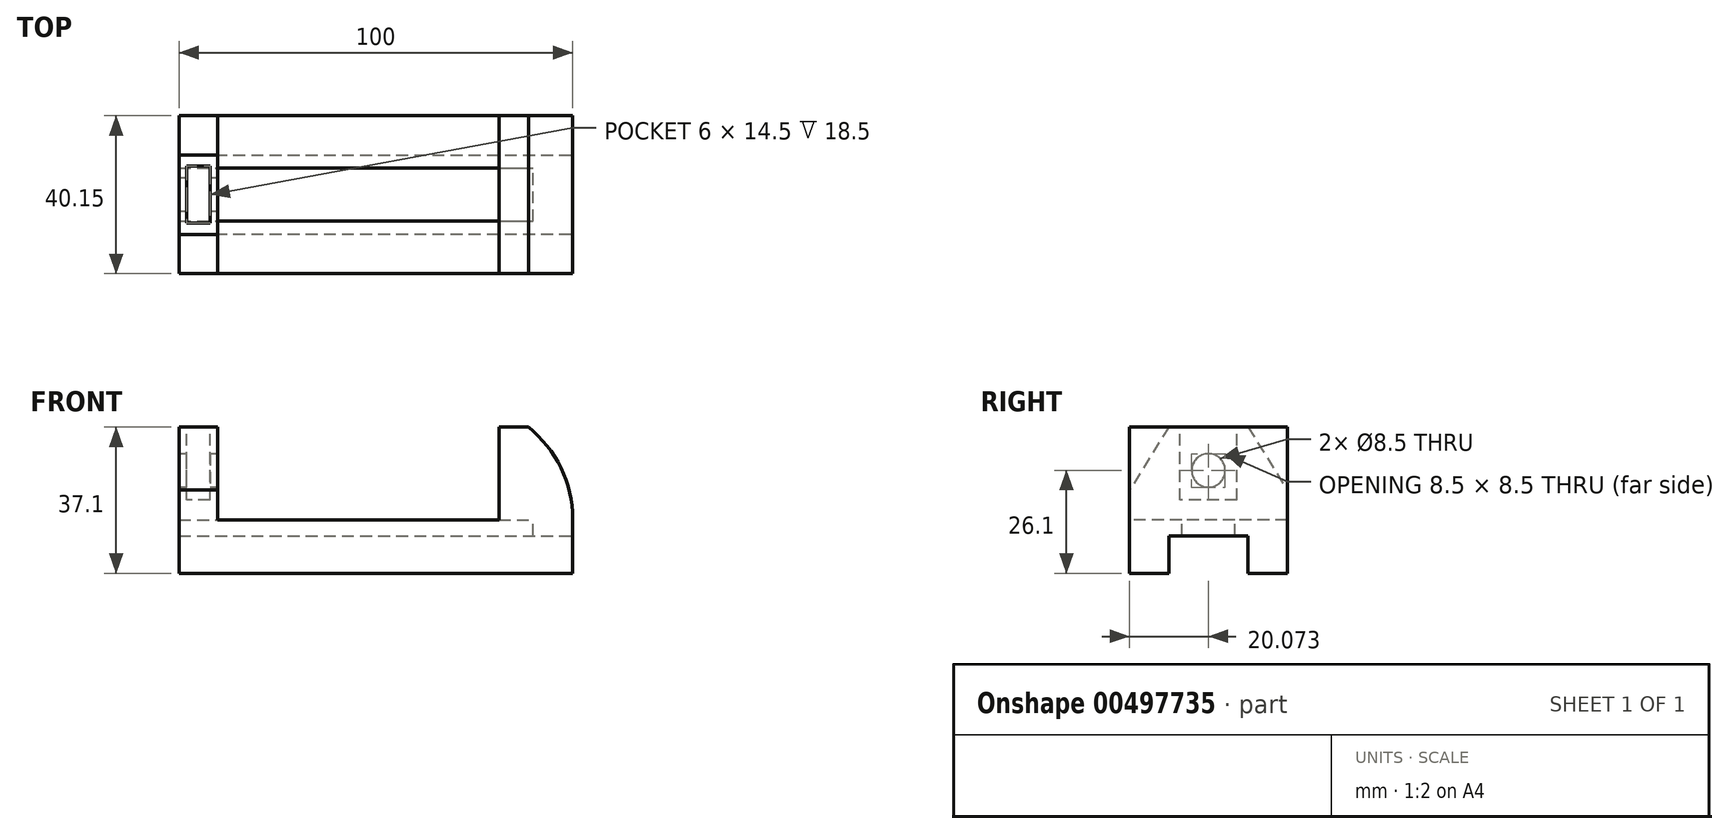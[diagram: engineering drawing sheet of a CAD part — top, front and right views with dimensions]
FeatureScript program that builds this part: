
annotation { "Feature Type Name" : "Feature", "Feature Type Description" : "" }
export const myFeature = defineFeature(function(context is Context, id is Id, definition is map)
    precondition{}
    {
        {
            var Q0;
            Q0=qCreatedBy(makeId("Top.planeOp"),FACE);
            var sketch = newSketch(context, id + "F0", { "sketchPlane" : qUnion([Q0])});
            skLineSegment(sketch, "E0.bottom", {"start": v(-62.81, 16.45) * mm, "end": v(37.19, 16.45) * mm});
            skLineSegment(sketch, "E0.top", {"start": v(-62.81, -23.7) * mm, "end": v(37.19, -23.7) * mm});
            skLineSegment(sketch, "E0.left", {"start": v(-62.81, 16.45) * mm, "end": v(-62.81, -23.7) * mm});
            skLineSegment(sketch, "E0.right", {"start": v(37.19, 16.45) * mm, "end": v(37.19, -23.7) * mm});
            skLineSegment(sketch, "E1", {"start": v(-62.81, -3.63) * mm, "end": v(37.19, -3.63) * mm, "construction": true});
            skLineSegment(sketch, "E2", {"start": v(-62.81, -3.63) * mm, "end": v(-62.81, 6.42) * mm, "construction": true});
            skLineSegment(sketch, "E3", {"start": v(-62.81, 6.42) * mm, "end": v(37.19, 6.42) * mm});
            skLineSegment(sketch, "E4", {"start": v(-62.81, 16.45) * mm, "end": v(-62.81, 3.12) * mm, "construction": true});
            skLineSegment(sketch, "E5", {"start": v(-62.81, 3.12) * mm, "end": v(37.19, 3.12) * mm});
            skLineSegment(sketch, "E6", {"start": v(-62.81, -3.63) * mm, "end": v(-53.01, -3.63) * mm, "construction": true});
            skLineSegment(sketch, "E7", {"start": v(-53.01, -3.63) * mm, "end": v(-53.01, 16.45) * mm});
            skLineSegment(sketch, "E8", {"start": v(37.19, -3.63) * mm, "end": v(18.44, -3.63) * mm, "construction": true});
            skLineSegment(sketch, "E9", {"start": v(18.44, -3.63) * mm, "end": v(18.44, 16.45) * mm});
            skLineSegment(sketch, "E10.MirrorCS", {"start": v(18.44, -3.63) * mm, "end": v(18.44, -23.7) * mm});
            skLineSegment(sketch, "E11.MirrorCS", {"start": v(-53.01, -3.63) * mm, "end": v(-53.01, -23.7) * mm});
            skLineSegment(sketch, "E12.MirrorCS", {"start": v(-62.81, -10.37) * mm, "end": v(37.19, -10.37) * mm});
            skLineSegment(sketch, "E13.MirrorCS", {"start": v(-62.81, -13.68) * mm, "end": v(37.19, -13.68) * mm});
            skLineSegment(sketch, "E14", {"start": v(37.19, -3.63) * mm, "end": v(27.19, -3.63) * mm, "construction": true});
            skLineSegment(sketch, "E15", {"start": v(27.19, -3.63) * mm, "end": v(27.19, -23.7) * mm});
            skLineSegment(sketch, "E16.MirrorCS", {"start": v(27.19, -3.63) * mm, "end": v(27.19, 16.45) * mm});
            skSolve(sketch);
        }
        {
            var Q0;
            {var subQ0=sQuery(id+"F0.wireOp",EDGE,"E12.MirrorCS");var subQ1=sQuery(id+"F0.wireOp",EDGE,"E0.right");var subQ2=makeQuery(id+"F0.imprint","INTERSECT",VERTEX,{"derivedFrom":[subQ1,subQ0]});Q0=makeQuery(id+"F0.imprint","IMPRINT",FACE,{"disambiguationData":[TD([[makeQuery(id+"F0.imprint","IMPRINT",EDGE,{"disambiguationData":[TD([[subQ2,-1.0]])],"derivedFrom":subQ1}),-1.0]])]});}
            var Q1;
            {var subQ0=sQuery(id+"F0.wireOp",EDGE,"E12.MirrorCS");var subQ1=sQuery(id+"F0.wireOp",EDGE,"E10.MirrorCS");var subQ2=makeQuery(id+"F0.imprint","INTERSECT",VERTEX,{"derivedFrom":[subQ1,subQ0]});Q1=makeQuery(id+"F0.imprint","IMPRINT",FACE,{"disambiguationData":[TD([[makeQuery(id+"F0.imprint","IMPRINT",EDGE,{"disambiguationData":[TD([[subQ2,-1.0]])],"derivedFrom":subQ1}),-1.0]])]});}
            var Q2;
            {var subQ0=sQuery(id+"F0.wireOp",EDGE,"E12.MirrorCS");var subQ1=sQuery(id+"F0.wireOp",EDGE,"E10.MirrorCS");var subQ2=makeQuery(id+"F0.imprint","INTERSECT",VERTEX,{"derivedFrom":[subQ1,subQ0]});Q2=makeQuery(id+"F0.imprint","IMPRINT",FACE,{"disambiguationData":[TD([[makeQuery(id+"F0.imprint","IMPRINT",EDGE,{"disambiguationData":[TD([[subQ2,-1.0]])],"derivedFrom":subQ1}),1.0]])]});}
            var Q3;
            {var subQ0=sQuery(id+"F0.wireOp",EDGE,"E10.MirrorCS");var subQ1=sQuery(id+"F0.wireOp",EDGE,"E0.top");var subQ2=makeQuery(id+"F0.imprint","INTERSECT",VERTEX,{"derivedFrom":[subQ1,subQ0]});Q3=makeQuery(id+"F0.imprint","IMPRINT",FACE,{"disambiguationData":[TD([[makeQuery(id+"F0.imprint","IMPRINT",EDGE,{"disambiguationData":[TD([[subQ2,-1.0]])],"derivedFrom":subQ1}),1.0]])]});}
            var Q4;
            {var subQ0=sQuery(id+"F0.wireOp",EDGE,"E0.right");var subQ1=sQuery(id+"F0.wireOp",EDGE,"E0.top");var subQ2=makeQuery(id+"F0.imprint","INTERSECT",VERTEX,{"derivedFrom":[subQ1,subQ0]});Q4=makeQuery(id+"F0.imprint","IMPRINT",FACE,{"disambiguationData":[TD([[makeQuery(id+"F0.imprint","IMPRINT",EDGE,{"disambiguationData":[TD([[subQ2,1.0]])],"derivedFrom":subQ1}),1.0]])]});}
            var Q5;
            {var subQ0=sQuery(id+"F0.wireOp",EDGE,"E10.MirrorCS");var subQ1=sQuery(id+"F0.wireOp",EDGE,"E0.top");var subQ2=makeQuery(id+"F0.imprint","INTERSECT",VERTEX,{"derivedFrom":[subQ1,subQ0]});Q5=makeQuery(id+"F0.imprint","IMPRINT",FACE,{"disambiguationData":[TD([[makeQuery(id+"F0.imprint","IMPRINT",EDGE,{"disambiguationData":[TD([[subQ2,1.0]])],"derivedFrom":subQ1}),1.0]])]});}
            var Q6;
            {var subQ0=sQuery(id+"F0.wireOp",EDGE,"E0.left");var subQ1=sQuery(id+"F0.wireOp",EDGE,"E0.top");var subQ2=makeQuery(id+"F0.imprint","INTERSECT",VERTEX,{"derivedFrom":[subQ1,subQ0]});Q6=makeQuery(id+"F0.imprint","IMPRINT",FACE,{"disambiguationData":[TD([[makeQuery(id+"F0.imprint","IMPRINT",EDGE,{"disambiguationData":[TD([[subQ2,-1.0]])],"derivedFrom":subQ1}),1.0]])]});}
            var Q7;
            {var subQ0=sQuery(id+"F0.wireOp",EDGE,"E12.MirrorCS");var subQ1=sQuery(id+"F0.wireOp",EDGE,"E0.left");var subQ2=makeQuery(id+"F0.imprint","INTERSECT",VERTEX,{"derivedFrom":[subQ1,subQ0]});Q7=makeQuery(id+"F0.imprint","IMPRINT",FACE,{"disambiguationData":[TD([[makeQuery(id+"F0.imprint","IMPRINT",EDGE,{"disambiguationData":[TD([[subQ2,-1.0]])],"derivedFrom":subQ1}),1.0]])]});}
            var Q8;
            {var subQ0=sQuery(id+"F0.wireOp",EDGE,"E3");var subQ1=sQuery(id+"F0.wireOp",EDGE,"E0.left");var subQ2=makeQuery(id+"F0.imprint","INTERSECT",VERTEX,{"derivedFrom":[subQ1,subQ0]});Q8=makeQuery(id+"F0.imprint","IMPRINT",FACE,{"disambiguationData":[TD([[makeQuery(id+"F0.imprint","IMPRINT",EDGE,{"disambiguationData":[TD([[subQ2,-1.0]])],"derivedFrom":subQ1}),1.0]])]});}
            var Q9;
            {var subQ0=sQuery(id+"F0.wireOp",EDGE,"E0.left");var subQ1=sQuery(id+"F0.wireOp",EDGE,"E0.bottom");var subQ2=makeQuery(id+"F0.imprint","INTERSECT",VERTEX,{"derivedFrom":[subQ1,subQ0]});Q9=makeQuery(id+"F0.imprint","IMPRINT",FACE,{"disambiguationData":[TD([[makeQuery(id+"F0.imprint","IMPRINT",EDGE,{"disambiguationData":[TD([[subQ2,-1.0]])],"derivedFrom":subQ1}),-1.0]])]});}
            var Q10;
            {var subQ0=sQuery(id+"F0.wireOp",EDGE,"E7");var subQ1=sQuery(id+"F0.wireOp",EDGE,"E0.bottom");var subQ2=makeQuery(id+"F0.imprint","INTERSECT",VERTEX,{"derivedFrom":[subQ1,subQ0]});Q10=makeQuery(id+"F0.imprint","IMPRINT",FACE,{"disambiguationData":[TD([[makeQuery(id+"F0.imprint","IMPRINT",EDGE,{"disambiguationData":[TD([[subQ2,-1.0]])],"derivedFrom":subQ1}),-1.0]])]});}
            var Q11;
            {var subQ0=sQuery(id+"F0.wireOp",EDGE,"E7");var subQ1=sQuery(id+"F0.wireOp",EDGE,"E3");var subQ2=makeQuery(id+"F0.imprint","INTERSECT",VERTEX,{"derivedFrom":[subQ1,subQ0]});Q11=makeQuery(id+"F0.imprint","IMPRINT",FACE,{"disambiguationData":[TD([[makeQuery(id+"F0.imprint","IMPRINT",EDGE,{"disambiguationData":[TD([[subQ2,-1.0]])],"derivedFrom":subQ1}),-1.0]])]});}
            var Q12;
            {var subQ0=sQuery(id+"F0.wireOp",EDGE,"E9");var subQ1=sQuery(id+"F0.wireOp",EDGE,"E0.bottom");var subQ2=makeQuery(id+"F0.imprint","INTERSECT",VERTEX,{"derivedFrom":[subQ1,subQ0]});Q12=makeQuery(id+"F0.imprint","IMPRINT",FACE,{"disambiguationData":[TD([[makeQuery(id+"F0.imprint","IMPRINT",EDGE,{"disambiguationData":[TD([[subQ2,-1.0]])],"derivedFrom":subQ1}),-1.0]])]});}
            var Q13;
            {var subQ0=sQuery(id+"F0.wireOp",EDGE,"E9");var subQ1=sQuery(id+"F0.wireOp",EDGE,"E3");var subQ2=makeQuery(id+"F0.imprint","INTERSECT",VERTEX,{"derivedFrom":[subQ1,subQ0]});Q13=makeQuery(id+"F0.imprint","IMPRINT",FACE,{"disambiguationData":[TD([[makeQuery(id+"F0.imprint","IMPRINT",EDGE,{"disambiguationData":[TD([[subQ2,-1.0]])],"derivedFrom":subQ1}),-1.0]])]});}
            var Q14;
            {var subQ0=sQuery(id+"F0.wireOp",EDGE,"E3");var subQ1=sQuery(id+"F0.wireOp",EDGE,"E0.right");var subQ2=makeQuery(id+"F0.imprint","INTERSECT",VERTEX,{"derivedFrom":[subQ1,subQ0]});Q14=makeQuery(id+"F0.imprint","IMPRINT",FACE,{"disambiguationData":[TD([[makeQuery(id+"F0.imprint","IMPRINT",EDGE,{"disambiguationData":[TD([[subQ2,-1.0]])],"derivedFrom":subQ1}),-1.0]])]});}
            var Q15;
            {var subQ0=sQuery(id+"F0.wireOp",EDGE,"E0.right");var subQ1=sQuery(id+"F0.wireOp",EDGE,"E0.bottom");var subQ2=makeQuery(id+"F0.imprint","INTERSECT",VERTEX,{"derivedFrom":[subQ1,subQ0]});Q15=makeQuery(id+"F0.imprint","IMPRINT",FACE,{"disambiguationData":[TD([[makeQuery(id+"F0.imprint","IMPRINT",EDGE,{"disambiguationData":[TD([[subQ2,1.0]])],"derivedFrom":subQ1}),-1.0]])]});}
            var Q16;
            {var subQ5=sQuery(id+"F0.wireOp",EDGE,"E0.right");var subQ7=sQuery(id+"F0.wireOp",EDGE,"E5");var subQ8=makeQuery(id+"F0.imprint","INTERSECT",VERTEX,{"derivedFrom":[subQ5,subQ7]});Q16=makeQuery(id+"F0.imprint","IMPRINT",FACE,{"disambiguationData":[TD([[makeQuery(id+"F0.imprint","IMPRINT",EDGE,{"disambiguationData":[TD([[subQ8,-1.0]])],"derivedFrom":subQ5}),-1.0]])]});}
            extrude(context, id + "F1", {"entities" : qUnion([Q0, Q1, Q2, Q3, Q4, Q5, Q6, Q7, Q8, Q9, Q10, Q11, Q12, Q13, Q14, Q15, Q16]), "oppositeDirection" : true, "depth" : 4 * mm});
        }
        {
            var Q0;
            {var subQ0=sQuery(id+"F0.wireOp",EDGE,"E0.left");var subQ1=sQuery(id+"F0.wireOp",EDGE,"E0.top");var subQ2=makeQuery(id+"F0.imprint","INTERSECT",VERTEX,{"derivedFrom":[subQ1,subQ0]});Q0=makeQuery(id+"F0.imprint","IMPRINT",FACE,{"disambiguationData":[TD([[makeQuery(id+"F0.imprint","IMPRINT",EDGE,{"disambiguationData":[TD([[subQ2,-1.0]])],"derivedFrom":subQ1}),1.0]])]});}
            var Q1;
            {var subQ0=sQuery(id+"F0.wireOp",EDGE,"E10.MirrorCS");var subQ1=sQuery(id+"F0.wireOp",EDGE,"E0.top");var subQ2=makeQuery(id+"F0.imprint","INTERSECT",VERTEX,{"derivedFrom":[subQ1,subQ0]});Q1=makeQuery(id+"F0.imprint","IMPRINT",FACE,{"disambiguationData":[TD([[makeQuery(id+"F0.imprint","IMPRINT",EDGE,{"disambiguationData":[TD([[subQ2,1.0]])],"derivedFrom":subQ1}),1.0]])]});}
            var Q2;
            {var subQ0=sQuery(id+"F0.wireOp",EDGE,"E10.MirrorCS");var subQ1=sQuery(id+"F0.wireOp",EDGE,"E0.top");var subQ2=makeQuery(id+"F0.imprint","INTERSECT",VERTEX,{"derivedFrom":[subQ1,subQ0]});Q2=makeQuery(id+"F0.imprint","IMPRINT",FACE,{"disambiguationData":[TD([[makeQuery(id+"F0.imprint","IMPRINT",EDGE,{"disambiguationData":[TD([[subQ2,-1.0]])],"derivedFrom":subQ1}),1.0]])]});}
            var Q3;
            {var subQ0=sQuery(id+"F0.wireOp",EDGE,"E0.right");var subQ1=sQuery(id+"F0.wireOp",EDGE,"E0.top");var subQ2=makeQuery(id+"F0.imprint","INTERSECT",VERTEX,{"derivedFrom":[subQ1,subQ0]});Q3=makeQuery(id+"F0.imprint","IMPRINT",FACE,{"disambiguationData":[TD([[makeQuery(id+"F0.imprint","IMPRINT",EDGE,{"disambiguationData":[TD([[subQ2,1.0]])],"derivedFrom":subQ1}),1.0]])]});}
            var Q4;
            {var subQ0=sQuery(id+"F0.wireOp",EDGE,"E0.right");var subQ1=sQuery(id+"F0.wireOp",EDGE,"E0.bottom");var subQ2=makeQuery(id+"F0.imprint","INTERSECT",VERTEX,{"derivedFrom":[subQ1,subQ0]});Q4=makeQuery(id+"F0.imprint","IMPRINT",FACE,{"disambiguationData":[TD([[makeQuery(id+"F0.imprint","IMPRINT",EDGE,{"disambiguationData":[TD([[subQ2,1.0]])],"derivedFrom":subQ1}),-1.0]])]});}
            var Q5;
            {var subQ0=sQuery(id+"F0.wireOp",EDGE,"E9");var subQ1=sQuery(id+"F0.wireOp",EDGE,"E0.bottom");var subQ2=makeQuery(id+"F0.imprint","INTERSECT",VERTEX,{"derivedFrom":[subQ1,subQ0]});Q5=makeQuery(id+"F0.imprint","IMPRINT",FACE,{"disambiguationData":[TD([[makeQuery(id+"F0.imprint","IMPRINT",EDGE,{"disambiguationData":[TD([[subQ2,-1.0]])],"derivedFrom":subQ1}),-1.0]])]});}
            var Q6;
            {var subQ0=sQuery(id+"F0.wireOp",EDGE,"E7");var subQ1=sQuery(id+"F0.wireOp",EDGE,"E0.bottom");var subQ2=makeQuery(id+"F0.imprint","INTERSECT",VERTEX,{"derivedFrom":[subQ1,subQ0]});Q6=makeQuery(id+"F0.imprint","IMPRINT",FACE,{"disambiguationData":[TD([[makeQuery(id+"F0.imprint","IMPRINT",EDGE,{"disambiguationData":[TD([[subQ2,-1.0]])],"derivedFrom":subQ1}),-1.0]])]});}
            var Q7;
            {var subQ0=sQuery(id+"F0.wireOp",EDGE,"E0.left");var subQ1=sQuery(id+"F0.wireOp",EDGE,"E0.bottom");var subQ2=makeQuery(id+"F0.imprint","INTERSECT",VERTEX,{"derivedFrom":[subQ1,subQ0]});Q7=makeQuery(id+"F0.imprint","IMPRINT",FACE,{"disambiguationData":[TD([[makeQuery(id+"F0.imprint","IMPRINT",EDGE,{"disambiguationData":[TD([[subQ2,-1.0]])],"derivedFrom":subQ1}),-1.0]])]});}
            extrude(context, id + "F2", {"entities" : qUnion([Q0, Q1, Q2, Q3, Q4, Q5, Q6, Q7]), "operationType" : NewBodyOperationType.ADD, "oppositeDirection" : true, "depth" : 13.5 * mm});
        }
        {
            var Q0;
            {var subQ3=sQuery(id+"F0.wireOp",EDGE,"E5");var subQ5=sQuery(id+"F0.wireOp",EDGE,"E0.left");var subQ6=makeQuery(id+"F0.imprint","INTERSECT",VERTEX,{"derivedFrom":[subQ5,subQ3]});Q0=makeQuery(id+"F0.imprint","IMPRINT",FACE,{"disambiguationData":[TD([[makeQuery(id+"F0.imprint","IMPRINT",EDGE,{"disambiguationData":[TD([[subQ6,-1.0]])],"derivedFrom":subQ5}),1.0]])]});}
            var Q1;
            {var subQ0=sQuery(id+"F0.wireOp",EDGE,"E12.MirrorCS");var subQ1=sQuery(id+"F0.wireOp",EDGE,"E0.left");var subQ2=makeQuery(id+"F0.imprint","INTERSECT",VERTEX,{"derivedFrom":[subQ1,subQ0]});Q1=makeQuery(id+"F0.imprint","IMPRINT",FACE,{"disambiguationData":[TD([[makeQuery(id+"F0.imprint","IMPRINT",EDGE,{"disambiguationData":[TD([[subQ2,-1.0]])],"derivedFrom":subQ1}),1.0]])]});}
            var Q2;
            {var subQ0=sQuery(id+"F0.wireOp",EDGE,"E0.left");var subQ1=sQuery(id+"F0.wireOp",EDGE,"E0.top");var subQ2=makeQuery(id+"F0.imprint","INTERSECT",VERTEX,{"derivedFrom":[subQ1,subQ0]});Q2=makeQuery(id+"F0.imprint","IMPRINT",FACE,{"disambiguationData":[TD([[makeQuery(id+"F0.imprint","IMPRINT",EDGE,{"disambiguationData":[TD([[subQ2,-1.0]])],"derivedFrom":subQ1}),1.0]])]});}
            var Q3;
            {var subQ0=sQuery(id+"F0.wireOp",EDGE,"E3");var subQ1=sQuery(id+"F0.wireOp",EDGE,"E0.left");var subQ2=makeQuery(id+"F0.imprint","INTERSECT",VERTEX,{"derivedFrom":[subQ1,subQ0]});Q3=makeQuery(id+"F0.imprint","IMPRINT",FACE,{"disambiguationData":[TD([[makeQuery(id+"F0.imprint","IMPRINT",EDGE,{"disambiguationData":[TD([[subQ2,-1.0]])],"derivedFrom":subQ1}),1.0]])]});}
            var Q4;
            {var subQ0=sQuery(id+"F0.wireOp",EDGE,"E0.left");var subQ1=sQuery(id+"F0.wireOp",EDGE,"E0.bottom");var subQ2=makeQuery(id+"F0.imprint","INTERSECT",VERTEX,{"derivedFrom":[subQ1,subQ0]});Q4=makeQuery(id+"F0.imprint","IMPRINT",FACE,{"disambiguationData":[TD([[makeQuery(id+"F0.imprint","IMPRINT",EDGE,{"disambiguationData":[TD([[subQ2,-1.0]])],"derivedFrom":subQ1}),-1.0]])]});}
            var Q5;
            {var subQ0=sQuery(id+"F0.wireOp",EDGE,"E0.right");var subQ1=sQuery(id+"F0.wireOp",EDGE,"E0.bottom");var subQ2=makeQuery(id+"F0.imprint","INTERSECT",VERTEX,{"derivedFrom":[subQ1,subQ0]});Q5=makeQuery(id+"F0.imprint","IMPRINT",FACE,{"disambiguationData":[TD([[makeQuery(id+"F0.imprint","IMPRINT",EDGE,{"disambiguationData":[TD([[subQ2,1.0]])],"derivedFrom":subQ1}),-1.0]])]});}
            var Q6;
            {var subQ0=sQuery(id+"F0.wireOp",EDGE,"E9");var subQ1=sQuery(id+"F0.wireOp",EDGE,"E3");var subQ2=makeQuery(id+"F0.imprint","INTERSECT",VERTEX,{"derivedFrom":[subQ1,subQ0]});Q6=makeQuery(id+"F0.imprint","IMPRINT",FACE,{"disambiguationData":[TD([[makeQuery(id+"F0.imprint","IMPRINT",EDGE,{"disambiguationData":[TD([[subQ2,-1.0]])],"derivedFrom":subQ1}),-1.0]])]});}
            var Q7;
            {var subQ0=sQuery(id+"F0.wireOp",EDGE,"E9");var subQ1=sQuery(id+"F0.wireOp",EDGE,"E0.bottom");var subQ2=makeQuery(id+"F0.imprint","INTERSECT",VERTEX,{"derivedFrom":[subQ1,subQ0]});Q7=makeQuery(id+"F0.imprint","IMPRINT",FACE,{"disambiguationData":[TD([[makeQuery(id+"F0.imprint","IMPRINT",EDGE,{"disambiguationData":[TD([[subQ2,-1.0]])],"derivedFrom":subQ1}),-1.0]])]});}
            var Q8;
            {var subQ5=sQuery(id+"F0.wireOp",EDGE,"E9");var subQ7=sQuery(id+"F0.wireOp",EDGE,"E5");var subQ8=makeQuery(id+"F0.imprint","INTERSECT",VERTEX,{"derivedFrom":[subQ7,subQ5]});Q8=makeQuery(id+"F0.imprint","IMPRINT",FACE,{"disambiguationData":[TD([[makeQuery(id+"F0.imprint","IMPRINT",EDGE,{"disambiguationData":[TD([[subQ8,-1.0]])],"derivedFrom":subQ7}),-1.0]])]});}
            var Q9;
            {var subQ0=sQuery(id+"F0.wireOp",EDGE,"E10.MirrorCS");var subQ1=sQuery(id+"F0.wireOp",EDGE,"E0.top");var subQ2=makeQuery(id+"F0.imprint","INTERSECT",VERTEX,{"derivedFrom":[subQ1,subQ0]});Q9=makeQuery(id+"F0.imprint","IMPRINT",FACE,{"disambiguationData":[TD([[makeQuery(id+"F0.imprint","IMPRINT",EDGE,{"disambiguationData":[TD([[subQ2,-1.0]])],"derivedFrom":subQ1}),1.0]])]});}
            var Q10;
            {var subQ0=sQuery(id+"F0.wireOp",EDGE,"E12.MirrorCS");var subQ1=sQuery(id+"F0.wireOp",EDGE,"E10.MirrorCS");var subQ2=makeQuery(id+"F0.imprint","INTERSECT",VERTEX,{"derivedFrom":[subQ1,subQ0]});Q10=makeQuery(id+"F0.imprint","IMPRINT",FACE,{"disambiguationData":[TD([[makeQuery(id+"F0.imprint","IMPRINT",EDGE,{"disambiguationData":[TD([[subQ2,-1.0]])],"derivedFrom":subQ1}),1.0]])]});}
            var Q11;
            {var subQ0=sQuery(id+"F0.wireOp",EDGE,"E0.right");var subQ1=sQuery(id+"F0.wireOp",EDGE,"E0.top");var subQ2=makeQuery(id+"F0.imprint","INTERSECT",VERTEX,{"derivedFrom":[subQ1,subQ0]});Q11=makeQuery(id+"F0.imprint","IMPRINT",FACE,{"disambiguationData":[TD([[makeQuery(id+"F0.imprint","IMPRINT",EDGE,{"disambiguationData":[TD([[subQ2,1.0]])],"derivedFrom":subQ1}),1.0]])]});}
            var Q12;
            {var subQ0=sQuery(id+"F0.wireOp",EDGE,"E12.MirrorCS");var subQ1=sQuery(id+"F0.wireOp",EDGE,"E0.right");var subQ2=makeQuery(id+"F0.imprint","INTERSECT",VERTEX,{"derivedFrom":[subQ1,subQ0]});Q12=makeQuery(id+"F0.imprint","IMPRINT",FACE,{"disambiguationData":[TD([[makeQuery(id+"F0.imprint","IMPRINT",EDGE,{"disambiguationData":[TD([[subQ2,-1.0]])],"derivedFrom":subQ1}),-1.0]])]});}
            var Q13;
            {var subQ5=sQuery(id+"F0.wireOp",EDGE,"E0.right");var subQ7=sQuery(id+"F0.wireOp",EDGE,"E5");var subQ8=makeQuery(id+"F0.imprint","INTERSECT",VERTEX,{"derivedFrom":[subQ5,subQ7]});Q13=makeQuery(id+"F0.imprint","IMPRINT",FACE,{"disambiguationData":[TD([[makeQuery(id+"F0.imprint","IMPRINT",EDGE,{"disambiguationData":[TD([[subQ8,-1.0]])],"derivedFrom":subQ5}),-1.0]])]});}
            var Q14;
            {var subQ0=sQuery(id+"F0.wireOp",EDGE,"E3");var subQ1=sQuery(id+"F0.wireOp",EDGE,"E0.right");var subQ2=makeQuery(id+"F0.imprint","INTERSECT",VERTEX,{"derivedFrom":[subQ1,subQ0]});Q14=makeQuery(id+"F0.imprint","IMPRINT",FACE,{"disambiguationData":[TD([[makeQuery(id+"F0.imprint","IMPRINT",EDGE,{"disambiguationData":[TD([[subQ2,-1.0]])],"derivedFrom":subQ1}),-1.0]])]});}
            extrude(context, id + "F3", {"entities" : qUnion([Q0, Q1, Q2, Q3, Q4, Q5, Q6, Q7, Q8, Q9, Q10, Q11, Q12, Q13, Q14]), "operationType" : NewBodyOperationType.ADD, "depth" : 23.6 * mm});
        }
        {
            var Q0;
            {var subQ0=sQuery(id+"F0.wireOp",EDGE,"E0.bottom");Q0=makeQuery(id+"F3.opExtrude","CAP_EDGE",EDGE,{"disambiguationData":[OSD([subQ0]),TDD([makeQuery(id+"F0.imprint","IMPRINT",EDGE,{"disambiguationData":[TD([[makeQuery(id+"F0.imprint","INTERSECT",VERTEX,{"derivedFrom":[subQ0,sQuery(id+"F0.wireOp",EDGE,"E0.left")]}),-1.0]])],"derivedFrom":subQ0})])],"isStart":false});}
            var Q1;
            {var subQ0=sQuery(id+"F0.wireOp",EDGE,"E0.top");Q1=makeQuery(id+"F3.opExtrude","CAP_EDGE",EDGE,{"disambiguationData":[OSD([subQ0]),TDD([makeQuery(id+"F0.imprint","IMPRINT",EDGE,{"disambiguationData":[TD([[makeQuery(id+"F0.imprint","INTERSECT",VERTEX,{"derivedFrom":[subQ0,sQuery(id+"F0.wireOp",EDGE,"E0.left")]}),-1.0]])],"derivedFrom":subQ0})])],"isStart":false});}
            chamfer(context, id + "F4", {"entities" : qUnion([Q0, Q1]), "chamferType" : ChamferType.TWO_OFFSETS, "width1" : 16 * mm, "oppositeDirection" : false, "width2" : 10 * mm, "tangentPropagation" : true});
        }
        {
            var Q0;
            {var subQ0=sQuery(id+"F0.wireOp",EDGE,"E0.bottom");Q0=makeQuery(id+"F3.boolean.opBoolean","MERGE",FACE,{"derivedFrom":[makeQuery(id+"F2.boolean.opBoolean","MERGE",FACE,{"derivedFrom":[makeQuery(id+"F1.opExtrude","SWEPT_FACE",FACE,{"disambiguationData":[OSD([subQ0])]}),makeQuery(id+"F2.opExtrude","SWEPT_FACE",FACE,{"disambiguationData":[OSD([subQ0])]})]}),makeQuery(id+"F3.opExtrude","SWEPT_FACE",FACE,{"disambiguationData":[OSD([subQ0]),TDD([makeQuery(id+"F0.imprint","IMPRINT",EDGE,{"disambiguationData":[TD([[makeQuery(id+"F0.imprint","INTERSECT",VERTEX,{"derivedFrom":[subQ0,sQuery(id+"F0.wireOp",EDGE,"E0.left")]}),-1.0]])],"derivedFrom":subQ0})])]}),makeQuery(id+"F3.opExtrude","SWEPT_FACE",FACE,{"disambiguationData":[OSD([subQ0]),TDD([makeQuery(id+"F0.imprint","IMPRINT",EDGE,{"disambiguationData":[TD([[makeQuery(id+"F0.imprint","INTERSECT",VERTEX,{"derivedFrom":[subQ0,sQuery(id+"F0.wireOp",EDGE,"E9")]}),-1.0]])],"derivedFrom":subQ0}),makeQuery(id+"F0.imprint","IMPRINT",EDGE,{"disambiguationData":[TD([[makeQuery(id+"F0.imprint","INTERSECT",VERTEX,{"derivedFrom":[subQ0,sQuery(id+"F0.wireOp",EDGE,"E0.right")]}),1.0]])],"derivedFrom":subQ0})])]})]});}
            var sketch = newSketch(context, id + "F5", { "sketchPlane" : qUnion([Q0])});
            skLineSegment(sketch, "E17", {"start": v(-18.44, 23.6) * mm, "end": v(-25.94, 23.6) * mm});
            skArc(sketch, "E18", {"start": v(-25.94, 23.6) * mm, "mid": v(-34.27, 13.09) * mm, "end": v(-37.19, 0) * mm});
            skSolve(sketch);
        }
        {
            var Q0;
            {var subQ0=sQuery(id+"F5.wireOp",EDGE,"E18");var subQ1=sQuery(id+"F0.wireOp",EDGE,"E0.right");var subQ2=sQuery(id+"F0.wireOp",EDGE,"E0.bottom");var subQ4=makeQuery(id+"F3.opExtrude","CAP_EDGE",EDGE,{"disambiguationData":[OSD([subQ2]),TDD([makeQuery(id+"F0.imprint","IMPRINT",EDGE,{"disambiguationData":[TD([[makeQuery(id+"F0.imprint","INTERSECT",VERTEX,{"derivedFrom":[subQ2,sQuery(id+"F0.wireOp",EDGE,"E9")]}),-1.0]])],"derivedFrom":subQ2}),makeQuery(id+"F0.imprint","IMPRINT",EDGE,{"disambiguationData":[TD([[makeQuery(id+"F0.imprint","INTERSECT",VERTEX,{"derivedFrom":[subQ2,subQ1]}),1.0]])],"derivedFrom":subQ2})])],"isStart":false});var subQ5=makeQuery(id+"F5.imprint","INTERSECT",VERTEX,{"derivedFrom":[subQ4,sQuery(id+"F5.wireOp",EDGE,"E17"),subQ0]});Q0=makeQuery(id+"F5.imprint","IMPRINT",FACE,{"disambiguationData":[TD([[makeQuery(id+"F5.imprint","IMPRINT",EDGE,{"disambiguationData":[TD([[subQ5,-1.0]])],"derivedFrom":subQ0}),-1.0]])]});}
            extrude(context, id + "F6", {"entities" : qUnion([Q0]), "operationType" : NewBodyOperationType.REMOVE, "endBound" : BoundingType.THROUGH_ALL, "oppositeDirection" : true, "depth" : 25 * mm});
        }
        {
            var Q0;
            {var subQ0=sQuery(id+"F0.wireOp",EDGE,"E0.left");var subQ2=makeQuery(id+"F0.imprint","IMPRINT",EDGE,{"disambiguationData":[TD([[makeQuery(id+"F0.imprint","INTERSECT",VERTEX,{"derivedFrom":[sQuery(id+"F0.wireOp",EDGE,"E0.top"),subQ0]}),1.0]])],"derivedFrom":subQ0});var subQ3=makeQuery(id+"F0.imprint","INTERSECT",VERTEX,{"derivedFrom":[subQ0,sQuery(id+"F0.wireOp",EDGE,"E3")]});var subQ4=makeQuery(id+"F0.imprint","IMPRINT",EDGE,{"disambiguationData":[TD([[makeQuery(id+"F0.imprint","INTERSECT",VERTEX,{"derivedFrom":[sQuery(id+"F0.wireOp",EDGE,"E0.bottom"),subQ0]}),-1.0]])],"derivedFrom":subQ0});Q0=makeQuery(id+"F3.boolean.opBoolean","MERGE",FACE,{"derivedFrom":[makeQuery(id+"F2.boolean.opBoolean","MERGE",FACE,{"derivedFrom":[makeQuery(id+"F1.opExtrude","SWEPT_FACE",FACE,{"disambiguationData":[OSD([subQ0]),TDD([subQ4,makeQuery(id+"F0.imprint","IMPRINT",EDGE,{"disambiguationData":[TD([[subQ3,-1.0]])],"derivedFrom":subQ0})])]}),makeQuery(id+"F2.opExtrude","SWEPT_FACE",FACE,{"disambiguationData":[OSD([subQ0]),TDD([subQ4])]})]}),makeQuery(id+"F2.boolean.opBoolean","MERGE",FACE,{"derivedFrom":[makeQuery(id+"F1.opExtrude","SWEPT_FACE",FACE,{"disambiguationData":[OSD([subQ0]),TDD([makeQuery(id+"F0.imprint","IMPRINT",EDGE,{"disambiguationData":[TD([[makeQuery(id+"F0.imprint","INTERSECT",VERTEX,{"derivedFrom":[subQ0,sQuery(id+"F0.wireOp",EDGE,"E12.MirrorCS")]}),-1.0]])],"derivedFrom":subQ0}),subQ2])]}),makeQuery(id+"F2.opExtrude","SWEPT_FACE",FACE,{"disambiguationData":[OSD([subQ0]),TDD([subQ2])]})]}),makeQuery(id+"F3.opExtrude","SWEPT_FACE",FACE,{"disambiguationData":[OSD([subQ0])]})]});}
            var sketch = newSketch(context, id + "F7", { "sketchPlane" : qUnion([Q0])});
            skLineSegment(sketch, "E19", {"start": v(3.63, 23.6) * mm, "end": v(3.63, 12.6) * mm, "construction": true});
            skCircle(sketch, "E20", {"center": v(3.63, 12.6) * mm, "radius": 4.25 * mm});
            skSolve(sketch);
        }
        {
            var Q0;
            Q0=makeQuery(id+"F7.imprint","IMPRINT",FACE,{"disambiguationData":[TD([[makeQuery(id+"F7.imprint","IMPRINT",EDGE,{"derivedFrom":sQuery(id+"F7.wireOp",EDGE,"E20")}),1.0]])]});
            extrude(context, id + "F8", {"entities" : qUnion([Q0]), "operationType" : NewBodyOperationType.REMOVE, "oppositeDirection" : true, "depth" : 25 * mm});
        }
        {
            var Q0;
            Q0=makeQuery(id+"F3.opExtrude","CAP_FACE",FACE,{"disambiguationData":[OSD([sQuery(id+"F0.wireOp",EDGE,"E0.bottom"),sQuery(id+"F0.wireOp",EDGE,"E0.top"),sQuery(id+"F0.wireOp",EDGE,"E0.left"),sQuery(id+"F0.wireOp",EDGE,"E7"),sQuery(id+"F0.wireOp",EDGE,"E11.MirrorCS")])],"isStart":false});
            var sketch = newSketch(context, id + "F9", { "sketchPlane" : qUnion([Q0])});
            skLineSegment(sketch, "E21", {"start": v(-57.91, 6.45) * mm, "end": v(-57.91, -13.7) * mm, "construction": true});
            skLineSegment(sketch, "E22", {"start": v(-53.01, -3.63) * mm, "end": v(-62.81, -3.63) * mm, "construction": true});
            skLineSegment(sketch, "E23", {"start": v(-57.91, -3.63) * mm, "end": v(-54.91, -3.63) * mm, "construction": true});
            skLineSegment(sketch, "E24", {"start": v(-54.91, -3.63) * mm, "end": v(-54.91, -10.88) * mm});
            skLineSegment(sketch, "E25", {"start": v(-54.91, -10.88) * mm, "end": v(-57.91, -10.88) * mm});
            skLineSegment(sketch, "E26.MirrorCS", {"start": v(-54.91, -3.63) * mm, "end": v(-54.91, 3.62) * mm});
            skLineSegment(sketch, "E27.MirrorCS", {"start": v(-54.91, 3.62) * mm, "end": v(-57.91, 3.62) * mm});
            skLineSegment(sketch, "E28.MirrorCS", {"start": v(-60.91, -10.88) * mm, "end": v(-57.91, -10.88) * mm});
            skLineSegment(sketch, "E29.MirrorCS", {"start": v(-60.91, -3.63) * mm, "end": v(-60.91, -10.88) * mm});
            skLineSegment(sketch, "E30.MirrorCS", {"start": v(-60.91, -3.63) * mm, "end": v(-60.91, 3.62) * mm});
            skLineSegment(sketch, "E31.MirrorCS", {"start": v(-60.91, 3.62) * mm, "end": v(-57.91, 3.62) * mm});
            skSolve(sketch);
        }
        {
            var Q0;
            Q0=makeQuery(id+"F9.imprint","IMPRINT",FACE,{"disambiguationData":[TD([[makeQuery(id+"F9.imprint","IMPRINT",EDGE,{"derivedFrom":sQuery(id+"F9.wireOp",EDGE,"E24")}),-1.0]])]});
            extrude(context, id + "F10", {"entities" : qUnion([Q0]), "operationType" : NewBodyOperationType.REMOVE, "oppositeDirection" : true, "depth" : 18.5 * mm});
        }
    });
